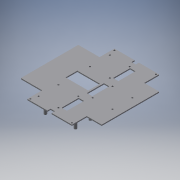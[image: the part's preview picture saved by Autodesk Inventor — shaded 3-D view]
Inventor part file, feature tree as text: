
AUTODESK INVENTOR PART (.ipt)
format: ipt  version: 2016 (Build 200138000, 138)  size: 284,672 bytes
history: native  units: in
note: dims shown in document units (in); Inventor stores cm internally (conversion verified against a paired STEP export)
features: extrude x9, sketch x9
ambient origin geometry x8: Origin, YZ Plane, XZ Plane, XY Plane, X Axis, Y Axis, Z Axis, Center Point
bodies: Solid1 (feature_tree)
feature tree (18):
  extrude  "Extrusion1"  Depth=4.252in
  extrude  "Extrusion2"  Depth=6.4567in
  extrude  "Extrusion3"  Depth=1.1024in
  extrude  "Extrusion4"  Depth=1.4961in
  extrude  "Extrusion5"  Depth=1.4961in
  extrude  "Extrusion6"  Depth=1.5748in
  extrude  "Extrusion7"  Depth=0.315in
  extrude  "Extrusion8"  Depth=0.0787in TaperAngle=0.0deg
  extrude  "Extrusion9"  Depth=0.3937in
  sketch  "Sketch3"  dims[d1=4.252in d2=4.252in]
  sketch  "Sketch7"  dims[d3=6.4567in d4=6.4567in]
  sketch  "Sketch8"  dims[d6=1.1024in d7=1.1024in]
  sketch  "Sketch9"  dims[d11=1.1024in d12=1.4961in]
  sketch  "Sketch10"  dims[d13=1.4961in d14=1.4961in]
  sketch  "Sketch11"  dims[d15=1.4961in d16=1.5748in]
  sketch  "Sketch12"  dims[d18=0.315in d19=0.315in]
  sketch  "Sketch13"  dims[d21=1.1024in d22=0.0787in d23=0.0in]
  sketch  "Sketch14"  dims[d24=2.0445in d25=1.0995in d26=1.9995in d27=1.8865in d28=0.1969in d29=0.1181in d30=0.1181in d31=0.1181in d32=0.1181in d33=0.1969in d34=0.1969in d35=0.1969in d36=0.5906in d37=0.0in d38=1.8865in d39=2.0445in d40=1.0995in d41=1.9995in d42=1.2865in d43=1.6995in d44=1.9995in d45=0.1181in d46=0.1181in d47=0.1181in d48=0.1181in d49=0.1969in d50=0.1969in d51=0.1969in d52=0.1969in d53=0.1969in d54=0.0in d55=0.1181in d56=0.1181in d57=0.1181in d58=0.3937in d59=0.0in d60=1.4685in d61=1.4685in d62=1.4685in d63=1.4685in d64=0.5906in d65=0.252in d66=0.252in d67=0.5906in d68=0.3937in d69=0.0in d70=1.4685in d71=1.4685in d72=1.4685in d73=1.4685in d74=0.5906in d75=0.5906in d78=0.3937in d79=0.0in d80=1.4685in d81=1.4685in d82=1.4685in d83=1.4685in d84=0.5906in d85=0.5906in d86=1.3917in d87=1.3917in d88=0.3937in d89=0.0in d90=0.3937in d91=1.2598in d92=0.1181in d93=1.2598in d94=0.3937in d95=0.1181in d97=0.1181in d98=0.1181in d99=1.2598in d100=0.1181in d101=0.1181in d102=0.3937in d103=0.3937in d104=0.0in d105=0.252in d106=0.252in d107=0.8661in d108=1.6732in d109=0.3937in d110=0.0in]
